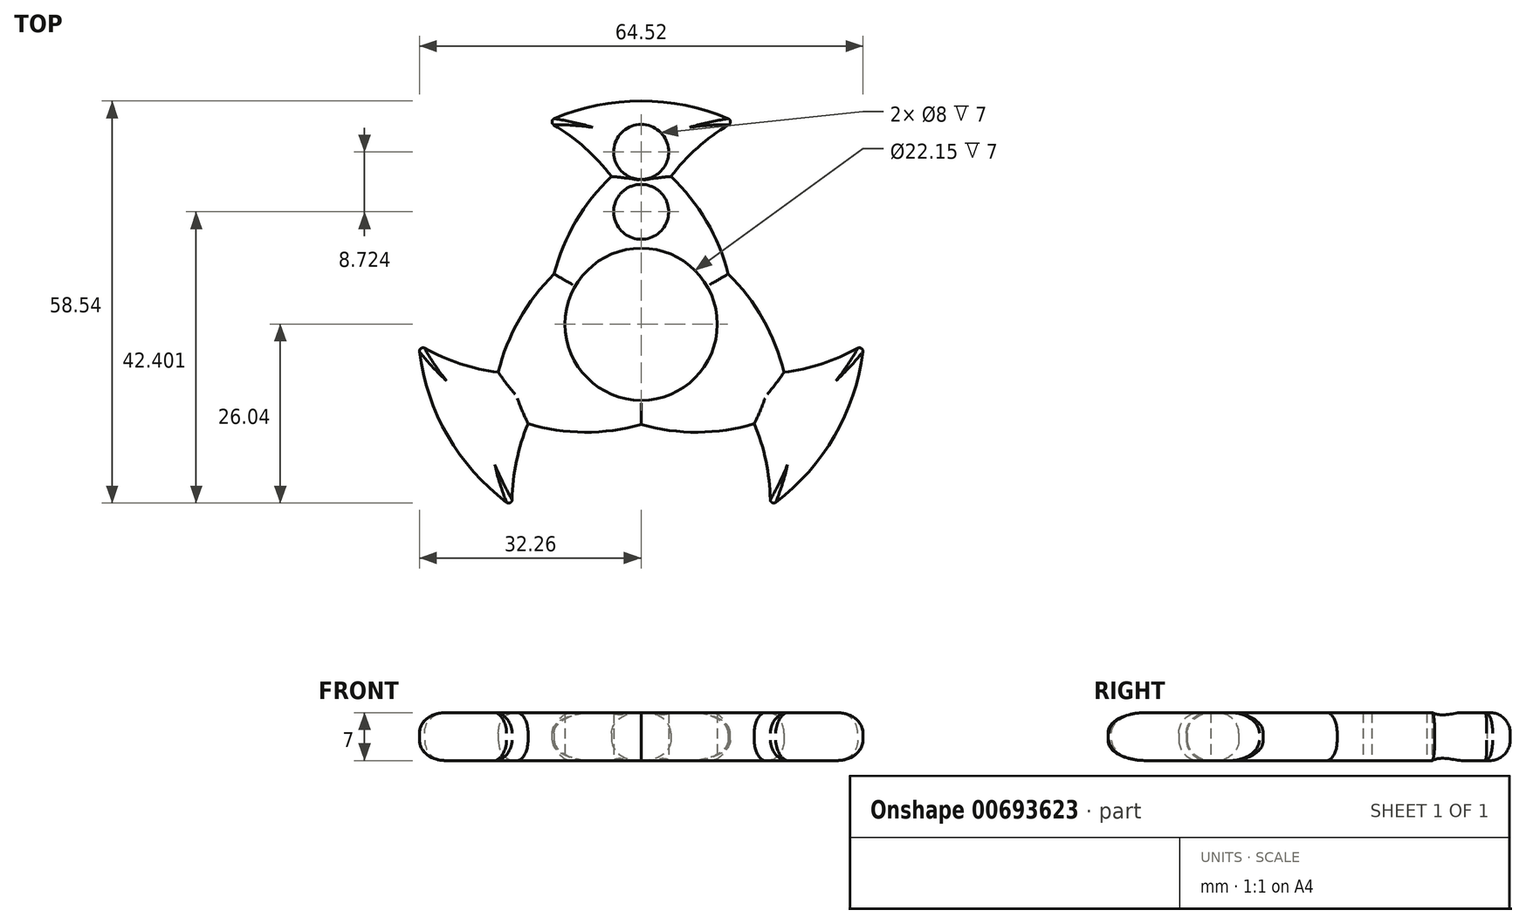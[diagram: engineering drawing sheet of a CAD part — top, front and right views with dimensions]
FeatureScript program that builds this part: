
annotation { "Feature Type Name" : "Feature", "Feature Type Description" : "" }
export const myFeature = defineFeature(function(context is Context, id is Id, definition is map)
    precondition{}
    {
        {
            var Q0;
            Q0=qCreatedBy(makeId("Top.planeOp"),FACE);
            var sketch = newSketch(context, id + "F0", { "sketchPlane" : qUnion([Q0])});
            skCircle(sketch, "E0", {"center": v(0, 0) * mm, "radius": 11.07 * mm});
            skLineSegment(sketch, "E1.bottom", {"start": v(-13.58, 0) * mm, "end": v(13.58, 0) * mm, "construction": true});
            skLineSegment(sketch, "E1.top", {"start": v(-13.58, 29.53) * mm, "end": v(13.57, 29.53) * mm, "construction": true});
            skLineSegment(sketch, "E1.left", {"start": v(-13.58, 0) * mm, "end": v(-13.58, 29.53) * mm, "construction": true});
            skLineSegment(sketch, "E1.right", {"start": v(13.58, 0) * mm, "end": v(13.57, 29.53) * mm, "construction": true});
            skArc(sketch, "E2", {"start": v(12.66, 7.3) * mm, "mid": v(9.5, 15) * mm, "end": v(4.33, 21.5) * mm});
            skArc(sketch, "E3", {"start": v(13.57, 29.53) * mm, "mid": v(0, 32.5) * mm, "end": v(-13.58, 29.53) * mm});
            skArc(sketch, "E4", {"start": v(-4.33, 21.5) * mm, "mid": v(-8.54, 26) * mm, "end": v(-13.57, 29.53) * mm});
            skPoint(sketch, "E4.startSnap0", {"position": v(0, 29.53) * mm});
            skArc(sketch, "E5", {"start": v(13.57, 29.53) * mm, "mid": v(8.54, 26) * mm, "end": v(4.33, 21.5) * mm});
            skArc(sketch, "E6.trimOffspring", {"start": v(-4.33, 21.5) * mm, "mid": v(-9.5, 15) * mm, "end": v(-12.66, 7.3) * mm});
            skPoint(sketch, "E7.orphan", {"position": v(0, 13.57) * mm});
            skArc(sketch, "E8.1.0", {"start": v(-32.36, -3) * mm, "mid": v(-28.15, -16.25) * mm, "end": v(-18.79, -26.52) * mm});
            skArc(sketch, "E8.1.1", {"start": v(-16.46, -14.5) * mm, "mid": v(-18.24, -20.4) * mm, "end": v(-18.79, -26.52) * mm});
            skArc(sketch, "E8.1.2", {"start": v(-32.36, -3) * mm, "mid": v(-26.78, -5.6) * mm, "end": v(-20.79, -7) * mm});
            skArc(sketch, "E8.1.3", {"start": v(-12.66, 7.3) * mm, "mid": v(-17.74, 0.73) * mm, "end": v(-20.79, -7) * mm});
            skArc(sketch, "E8.1.4", {"start": v(-16.46, -14.5) * mm, "mid": v(-8.24, -15.73) * mm, "end": v(0, -14.62) * mm});
            skArc(sketch, "E8.2.0", {"start": v(18.79, -26.52) * mm, "mid": v(28.15, -16.25) * mm, "end": v(32.36, -3) * mm});
            skArc(sketch, "E8.2.1", {"start": v(20.79, -7) * mm, "mid": v(26.78, -5.6) * mm, "end": v(32.36, -3) * mm});
            skArc(sketch, "E8.2.2", {"start": v(18.79, -26.52) * mm, "mid": v(18.24, -20.4) * mm, "end": v(16.46, -14.5) * mm});
            skArc(sketch, "E8.2.3", {"start": v(0, -14.62) * mm, "mid": v(8.24, -15.73) * mm, "end": v(16.46, -14.5) * mm});
            skArc(sketch, "E8.2.4", {"start": v(20.79, -7) * mm, "mid": v(17.74, 0.73) * mm, "end": v(12.66, 7.3) * mm});
            skPoint(sketch, "E9.orphan", {"position": v(-6.79, 11.76) * mm});
            skPoint(sketch, "E10.orphan", {"position": v(6.79, 11.76) * mm});
            skPoint(sketch, "E11.orphan", {"position": v(6.79, -11.76) * mm});
            skPoint(sketch, "E12.orphan", {"position": v(-6.79, -11.76) * mm});
            skSolve(sketch);
        }
        {
            var Q0;
            Q0 = qSketchRegion(id + "F0", true);
            extrude(context, id + "F1", {"entities" : qUnion([Q0]), "depth" : 7 * mm, "offsetDistance" : 25 * mm});
        }
        {
            var Q0;
            Q0=makeQuery(id+"F1.opExtrude","CAP_EDGE",EDGE,{"disambiguationData":[OSD([sQuery(id+"F0.wireOp",EDGE,"E3")])],"isStart":false});
            var Q1;
            Q1=makeQuery(id+"F1.opExtrude","CAP_EDGE",EDGE,{"disambiguationData":[OSD([sQuery(id+"F0.wireOp",EDGE,"E4")])],"isStart":false});
            var Q2;
            Q2=makeQuery(id+"F1.opExtrude","CAP_EDGE",EDGE,{"disambiguationData":[OSD([sQuery(id+"F0.wireOp",EDGE,"E6.trimOffspring")])],"isStart":false});
            var Q3;
            Q3=makeQuery(id+"F1.opExtrude","CAP_EDGE",EDGE,{"disambiguationData":[OSD([sQuery(id+"F0.wireOp",EDGE,"E8.1.3")])],"isStart":false});
            var Q4;
            Q4=makeQuery(id+"F1.opExtrude","CAP_EDGE",EDGE,{"disambiguationData":[OSD([sQuery(id+"F0.wireOp",EDGE,"E8.1.2")])],"isStart":false});
            var Q5;
            Q5=makeQuery(id+"F1.opExtrude","CAP_EDGE",EDGE,{"disambiguationData":[OSD([sQuery(id+"F0.wireOp",EDGE,"E8.1.0")])],"isStart":false});
            var Q6;
            Q6=makeQuery(id+"F1.opExtrude","CAP_EDGE",EDGE,{"disambiguationData":[OSD([sQuery(id+"F0.wireOp",EDGE,"E8.1.1")])],"isStart":false});
            var Q7;
            Q7=makeQuery(id+"F1.opExtrude","CAP_EDGE",EDGE,{"disambiguationData":[OSD([sQuery(id+"F0.wireOp",EDGE,"E8.1.4")])],"isStart":false});
            var Q8;
            Q8=makeQuery(id+"F1.opExtrude","CAP_EDGE",EDGE,{"disambiguationData":[OSD([sQuery(id+"F0.wireOp",EDGE,"E8.2.3")])],"isStart":false});
            var Q9;
            Q9=makeQuery(id+"F1.opExtrude","CAP_EDGE",EDGE,{"disambiguationData":[OSD([sQuery(id+"F0.wireOp",EDGE,"E8.2.2")])],"isStart":false});
            var Q10;
            Q10=makeQuery(id+"F1.opExtrude","CAP_EDGE",EDGE,{"disambiguationData":[OSD([sQuery(id+"F0.wireOp",EDGE,"E8.2.0")])],"isStart":false});
            var Q11;
            Q11=makeQuery(id+"F1.opExtrude","CAP_EDGE",EDGE,{"disambiguationData":[OSD([sQuery(id+"F0.wireOp",EDGE,"E8.2.1")])],"isStart":false});
            var Q12;
            Q12=makeQuery(id+"F1.opExtrude","CAP_EDGE",EDGE,{"disambiguationData":[OSD([sQuery(id+"F0.wireOp",EDGE,"E8.2.4")])],"isStart":false});
            var Q13;
            Q13=makeQuery(id+"F1.opExtrude","CAP_EDGE",EDGE,{"disambiguationData":[OSD([sQuery(id+"F0.wireOp",EDGE,"E2")])],"isStart":false});
            var Q14;
            Q14=makeQuery(id+"F1.opExtrude","CAP_EDGE",EDGE,{"disambiguationData":[OSD([sQuery(id+"F0.wireOp",EDGE,"E5")])],"isStart":false});
            var Q15;
            Q15=makeQuery(id+"F1.opExtrude","CAP_EDGE",EDGE,{"disambiguationData":[OSD([sQuery(id+"F0.wireOp",EDGE,"E2")])],"isStart":true});
            var Q16;
            Q16=makeQuery(id+"F1.opExtrude","CAP_EDGE",EDGE,{"disambiguationData":[OSD([sQuery(id+"F0.wireOp",EDGE,"E8.2.4")])],"isStart":true});
            var Q17;
            Q17=makeQuery(id+"F1.opExtrude","CAP_EDGE",EDGE,{"disambiguationData":[OSD([sQuery(id+"F0.wireOp",EDGE,"E8.2.1")])],"isStart":true});
            var Q18;
            Q18=makeQuery(id+"F1.opExtrude","CAP_EDGE",EDGE,{"disambiguationData":[OSD([sQuery(id+"F0.wireOp",EDGE,"E5")])],"isStart":true});
            var Q19;
            Q19=makeQuery(id+"F1.opExtrude","CAP_EDGE",EDGE,{"disambiguationData":[OSD([sQuery(id+"F0.wireOp",EDGE,"E3")])],"isStart":true});
            var Q20;
            Q20=makeQuery(id+"F1.opExtrude","CAP_EDGE",EDGE,{"disambiguationData":[OSD([sQuery(id+"F0.wireOp",EDGE,"E4")])],"isStart":true});
            var Q21;
            Q21=makeQuery(id+"F1.opExtrude","CAP_EDGE",EDGE,{"disambiguationData":[OSD([sQuery(id+"F0.wireOp",EDGE,"E6.trimOffspring")])],"isStart":true});
            var Q22;
            Q22=makeQuery(id+"F1.opExtrude","CAP_EDGE",EDGE,{"disambiguationData":[OSD([sQuery(id+"F0.wireOp",EDGE,"E8.1.3")])],"isStart":true});
            var Q23;
            Q23=makeQuery(id+"F1.opExtrude","CAP_EDGE",EDGE,{"disambiguationData":[OSD([sQuery(id+"F0.wireOp",EDGE,"E8.1.2")])],"isStart":true});
            var Q24;
            Q24=makeQuery(id+"F1.opExtrude","CAP_EDGE",EDGE,{"disambiguationData":[OSD([sQuery(id+"F0.wireOp",EDGE,"E8.1.0")])],"isStart":true});
            var Q25;
            Q25=makeQuery(id+"F1.opExtrude","CAP_EDGE",EDGE,{"disambiguationData":[OSD([sQuery(id+"F0.wireOp",EDGE,"E8.1.1")])],"isStart":true});
            var Q26;
            Q26=makeQuery(id+"F1.opExtrude","CAP_EDGE",EDGE,{"disambiguationData":[OSD([sQuery(id+"F0.wireOp",EDGE,"E8.1.4")])],"isStart":true});
            var Q27;
            Q27=makeQuery(id+"F1.opExtrude","CAP_EDGE",EDGE,{"disambiguationData":[OSD([sQuery(id+"F0.wireOp",EDGE,"E8.2.3")])],"isStart":true});
            var Q28;
            Q28=makeQuery(id+"F1.opExtrude","CAP_EDGE",EDGE,{"disambiguationData":[OSD([sQuery(id+"F0.wireOp",EDGE,"E8.2.2")])],"isStart":true});
            var Q29;
            Q29=makeQuery(id+"F1.opExtrude","CAP_EDGE",EDGE,{"disambiguationData":[OSD([sQuery(id+"F0.wireOp",EDGE,"E8.2.0")])],"isStart":true});
            fillet(context, id + "F2", {"entities" : qUnion([Q0, Q1, Q2, Q3, Q4, Q5, Q6, Q7, Q8, Q9, Q10, Q11, Q12, Q13, Q14, Q15, Q16, Q17, Q18, Q19, Q20, Q21, Q22, Q23, Q24, Q25, Q26, Q27, Q28, Q29]), "radius" : 3 * mm, "tangentPropagation" : true, "allowEdgeOverflow" : false});
        }
        {
            var Q0;
            Q0=makeQuery(id+"F1.opExtrude","SWEPT_EDGE",EDGE,{"disambiguationData":[OSD([sQuery(id+"F0.wireOp",EDGE,"E3"),sQuery(id+"F0.wireOp",EDGE,"E4")])]});
            var Q1;
            Q1=makeQuery(id+"F1.opExtrude","SWEPT_EDGE",EDGE,{"disambiguationData":[OSD([sQuery(id+"F0.wireOp",EDGE,"E8.1.0"),sQuery(id+"F0.wireOp",EDGE,"E8.1.2")])]});
            var Q2;
            Q2=makeQuery(id+"F1.opExtrude","SWEPT_EDGE",EDGE,{"disambiguationData":[OSD([sQuery(id+"F0.wireOp",EDGE,"E8.1.0"),sQuery(id+"F0.wireOp",EDGE,"E8.1.1")])]});
            var Q3;
            Q3=makeQuery(id+"F1.opExtrude","SWEPT_EDGE",EDGE,{"disambiguationData":[OSD([sQuery(id+"F0.wireOp",EDGE,"E8.2.0"),sQuery(id+"F0.wireOp",EDGE,"E8.2.2")])]});
            var Q4;
            Q4=makeQuery(id+"F1.opExtrude","SWEPT_EDGE",EDGE,{"disambiguationData":[OSD([sQuery(id+"F0.wireOp",EDGE,"E8.2.0"),sQuery(id+"F0.wireOp",EDGE,"E8.2.1")])]});
            var Q5;
            Q5=makeQuery(id+"F1.opExtrude","SWEPT_EDGE",EDGE,{"disambiguationData":[OSD([sQuery(id+"F0.wireOp",EDGE,"E3"),sQuery(id+"F0.wireOp",EDGE,"E5")])]});
            fillet(context, id + "F3", {"entities" : qUnion([Q0, Q1, Q2, Q3, Q4, Q5]), "radius" : 0.5 * mm, "tangentPropagation" : true, "allowEdgeOverflow" : false});
        }
        {
            var Q0;
            Q0=makeQuery(id+"F1.opExtrude","CAP_FACE",FACE,{"disambiguationData":[OSD([sQuery(id+"F0.wireOp",EDGE,"E0"),sQuery(id+"F0.wireOp",EDGE,"E2"),sQuery(id+"F0.wireOp",EDGE,"E3"),sQuery(id+"F0.wireOp",EDGE,"E4"),sQuery(id+"F0.wireOp",EDGE,"E5"),sQuery(id+"F0.wireOp",EDGE,"E6.trimOffspring"),sQuery(id+"F0.wireOp",EDGE,"E8.1.0"),sQuery(id+"F0.wireOp",EDGE,"E8.1.1"),sQuery(id+"F0.wireOp",EDGE,"E8.1.2"),sQuery(id+"F0.wireOp",EDGE,"E8.1.3"),sQuery(id+"F0.wireOp",EDGE,"E8.1.4"),sQuery(id+"F0.wireOp",EDGE,"E8.2.0"),sQuery(id+"F0.wireOp",EDGE,"E8.2.1"),sQuery(id+"F0.wireOp",EDGE,"E8.2.2"),sQuery(id+"F0.wireOp",EDGE,"E8.2.3"),sQuery(id+"F0.wireOp",EDGE,"E8.2.4")])],"isStart":true});
            var sketch = newSketch(context, id + "F4", { "sketchPlane" : qUnion([Q0])});
            skLineSegment(sketch, "E13", {"start": v(0, -29.5) * mm, "end": v(0, -11.07) * mm, "construction": true});
            skLineSegment(sketch, "E14", {"start": v(-3.38, -25.08) * mm, "end": v(3.38, -25.08) * mm, "construction": true});
            skPoint(sketch, "E15", {"position": v(0, -15.21) * mm});
            skPoint(sketch, "E16", {"position": v(0, -25.08) * mm});
            skLineSegment(sketch, "E17.0", {"start": v(6.47, -16.36) * mm, "end": v(-6.47, -16.36) * mm, "construction": true});
            skPoint(sketch, "E18", {"position": v(0, -16.36) * mm});
            skPoint(sketch, "E19.orphan", {"position": v(-6.47, -15.21) * mm});
            skPoint(sketch, "E20.0.start.orphan", {"position": v(6.47, -15.21) * mm});
            skSolve(sketch);
        }
        {
            var Q0;
            Q0=qCreatedBy(makeId("Right.planeOp"),FACE);
            var sketch = newSketch(context, id + "F5", { "sketchPlane" : qUnion([Q0])});
            skLineSegment(sketch, "E21", {"start": v(0, 38.56) * mm, "end": v(0, -27.67) * mm});
            skSolve(sketch);
        }
        {
            var Q0;
            Q0=sQuery(id+"F4.wireOp",VERTEX,"E16");
            var Q1;
            Q1=sQuery(id+"F4.wireOp",VERTEX,"E18");
            var Q2;
            Q2=makeQuery(id+"F1.opExtrude","SWEPT_BODY",BODY,{"disambiguationData":[OSD([sQuery(id+"F0.wireOp",EDGE,"E0"),sQuery(id+"F0.wireOp",EDGE,"E2"),sQuery(id+"F0.wireOp",EDGE,"E3"),sQuery(id+"F0.wireOp",EDGE,"E4"),sQuery(id+"F0.wireOp",EDGE,"E5"),sQuery(id+"F0.wireOp",EDGE,"E6.trimOffspring"),sQuery(id+"F0.wireOp",EDGE,"E8.1.0"),sQuery(id+"F0.wireOp",EDGE,"E8.1.1"),sQuery(id+"F0.wireOp",EDGE,"E8.1.2"),sQuery(id+"F0.wireOp",EDGE,"E8.1.3"),sQuery(id+"F0.wireOp",EDGE,"E8.1.4"),sQuery(id+"F0.wireOp",EDGE,"E8.2.0"),sQuery(id+"F0.wireOp",EDGE,"E8.2.1"),sQuery(id+"F0.wireOp",EDGE,"E8.2.2"),sQuery(id+"F0.wireOp",EDGE,"E8.2.3"),sQuery(id+"F0.wireOp",EDGE,"E8.2.4")])]});
            hole(context, id + "F6", {"style" : HoleStyle.SIMPLE, "endStyle" : HoleEndStyle.THROUGH, "holeDiameter" : 8 * mm, "majorDiameter" : 5 * mm, "isTappedThrough" : true, "tappedDepth" : 12 * mm, "tapClearance" : 3, "startFromSketch" : true, "locations" : qUnion([Q0, Q1]), "scope" : qUnion([Q2])});
        }
    });
